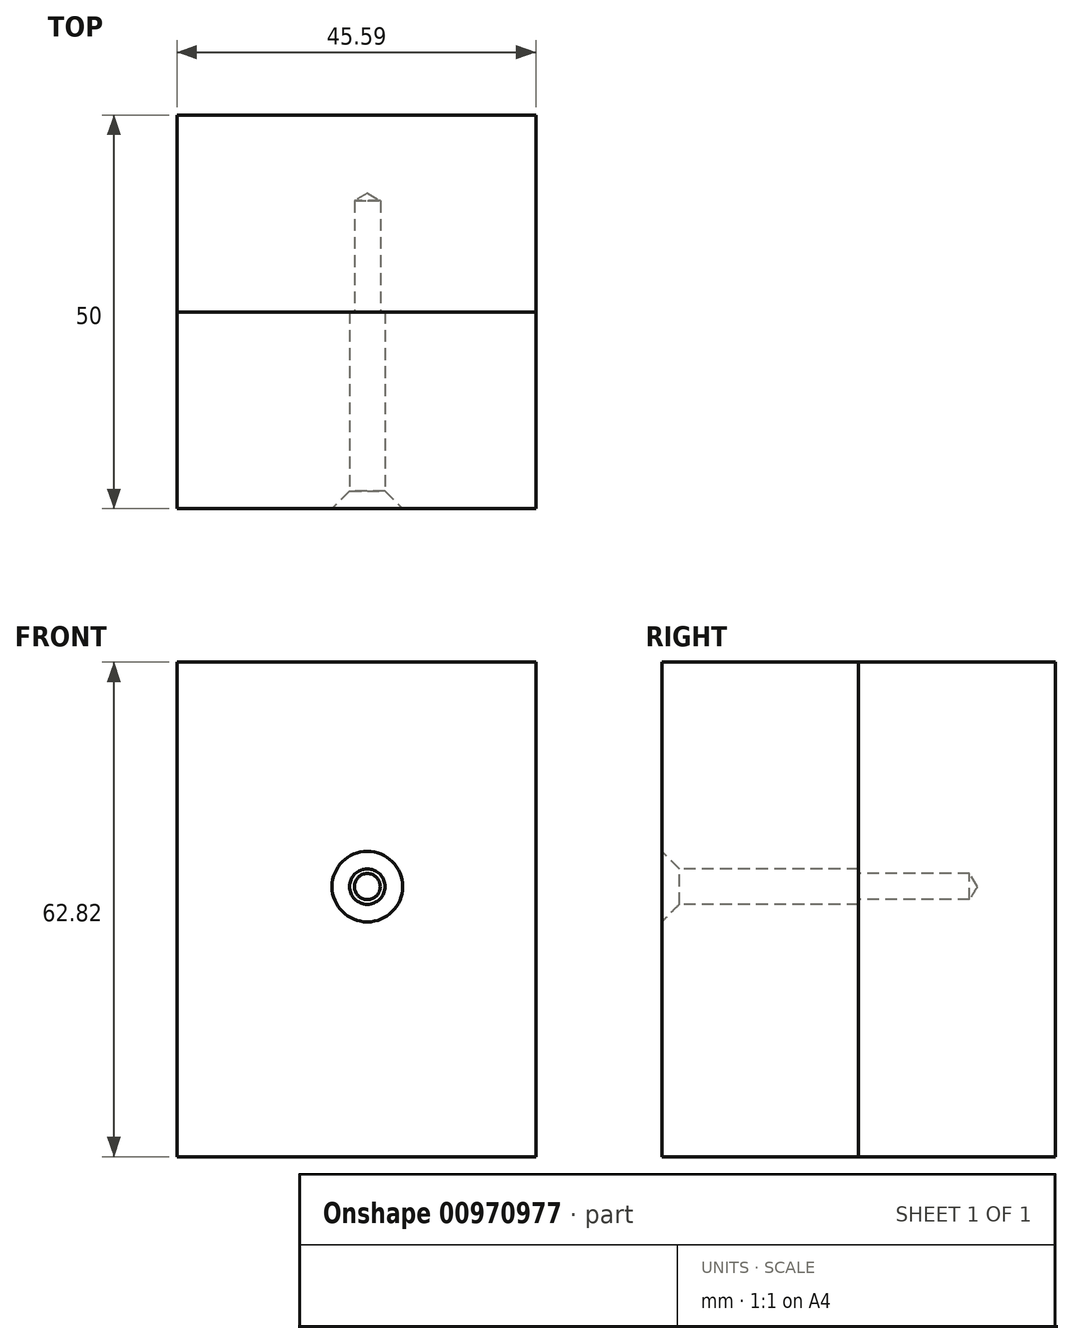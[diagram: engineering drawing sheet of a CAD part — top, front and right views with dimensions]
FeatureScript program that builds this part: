
annotation { "Feature Type Name" : "Feature", "Feature Type Description" : "" }
export const myFeature = defineFeature(function(context is Context, id is Id, definition is map)
    precondition{}
    {
        {
            var Q0;
            Q0=qCreatedBy(makeId("Front.planeOp"),FACE);
            var sketch = newSketch(context, id + "F0", { "sketchPlane" : qUnion([Q0])});
            skLineSegment(sketch, "E0.bottom", {"start": v(-106.23, 18.58) * mm, "end": v(-60.64, 18.58) * mm});
            skLineSegment(sketch, "E0.top", {"start": v(-106.23, -44.24) * mm, "end": v(-60.64, -44.24) * mm});
            skLineSegment(sketch, "E0.left", {"start": v(-106.23, 18.58) * mm, "end": v(-106.23, -44.24) * mm});
            skLineSegment(sketch, "E0.right", {"start": v(-60.64, 18.58) * mm, "end": v(-60.64, -44.24) * mm});
            skSolve(sketch);
        }
        {
            var Q0;
            Q0 = qSketchRegion(id + "F0", true);
            extrude(context, id + "F1", {"entities" : qUnion([Q0]), "depth" : 25 * mm, "offsetDistance" : 25 * mm});
        }
        {
            var Q0;
            Q0=makeQuery(id+"F1.opExtrude","CAP_FACE",FACE,{"disambiguationData":[OSD([sQuery(id+"F0.wireOp",EDGE,"E0.bottom"),sQuery(id+"F0.wireOp",EDGE,"E0.top"),sQuery(id+"F0.wireOp",EDGE,"E0.left"),sQuery(id+"F0.wireOp",EDGE,"E0.right")])],"isStart":false});
            extrude(context, id + "F2", {"entities" : qUnion([Q0]), "depth" : 25 * mm, "offsetDistance" : 25 * mm});
        }
        {
            var Q0;
            Q0=makeQuery(id+"F2.opExtrude","CAP_FACE",FACE,{"disambiguationData":[OSD([sQuery(id+"F0.wireOp",EDGE,"E0.bottom"),sQuery(id+"F0.wireOp",EDGE,"E0.top"),sQuery(id+"F0.wireOp",EDGE,"E0.left"),sQuery(id+"F0.wireOp",EDGE,"E0.right")])],"isStart":false});
            var sketch = newSketch(context, id + "F3", { "sketchPlane" : qUnion([Q0])});
            skPoint(sketch, "E1", {"position": v(-82.04, -9.93) * mm});
            skSolve(sketch);
        }
        {
            var Q0;
            Q0=sQuery(id+"F3.wireOp",VERTEX,"E1");
            var Q1;
            Q1=makeQuery(id+"F1.opExtrude","SWEPT_BODY",BODY,{"disambiguationData":[OSD([sQuery(id+"F0.wireOp",EDGE,"E0.bottom"),sQuery(id+"F0.wireOp",EDGE,"E0.top"),sQuery(id+"F0.wireOp",EDGE,"E0.left"),sQuery(id+"F0.wireOp",EDGE,"E0.right")])]});
            var Q2;
            Q2=makeQuery(id+"F2.opExtrude","SWEPT_BODY",BODY,{"disambiguationData":[OSD([sQuery(id+"F0.wireOp",EDGE,"E0.bottom"),sQuery(id+"F0.wireOp",EDGE,"E0.top"),sQuery(id+"F0.wireOp",EDGE,"E0.left"),sQuery(id+"F0.wireOp",EDGE,"E0.right")])]});
            hole(context, id + "F4", {"style" : HoleStyle.C_SINK, "endStyle" : HoleEndStyle.BLIND_IN_LAST, "standardTappedOrClearance" : lookupTablePath({ "fit" : "Normal", "standard" : "ISO", "size" : "M4", "type" : "Clearance" }), "standardBlindInLast" : lookupTablePath({ "fit" : "Normal", "standard" : "ISO", "engagement" : "75%", "pitch" : "0.7 mm", "size" : "M4", "type" : "Clearance & tapped" }), "holeDiameter" : 4.5 * mm, "cSinkDiameter" : 8.96 * mm, "cSinkAngle" : 90 * degree, "tapDrillDiameter" : 3.3 * mm, "majorDiameter" : 4 * mm, "showTappedDepth" : true, "holeDepth" : 14.1 * mm, "isTappedThrough" : true, "tappedDepth" : 12 * mm, "tapClearance" : 3, "locations" : qUnion([Q0]), "scope" : qUnion([Q1, Q2])});
        }
    });
